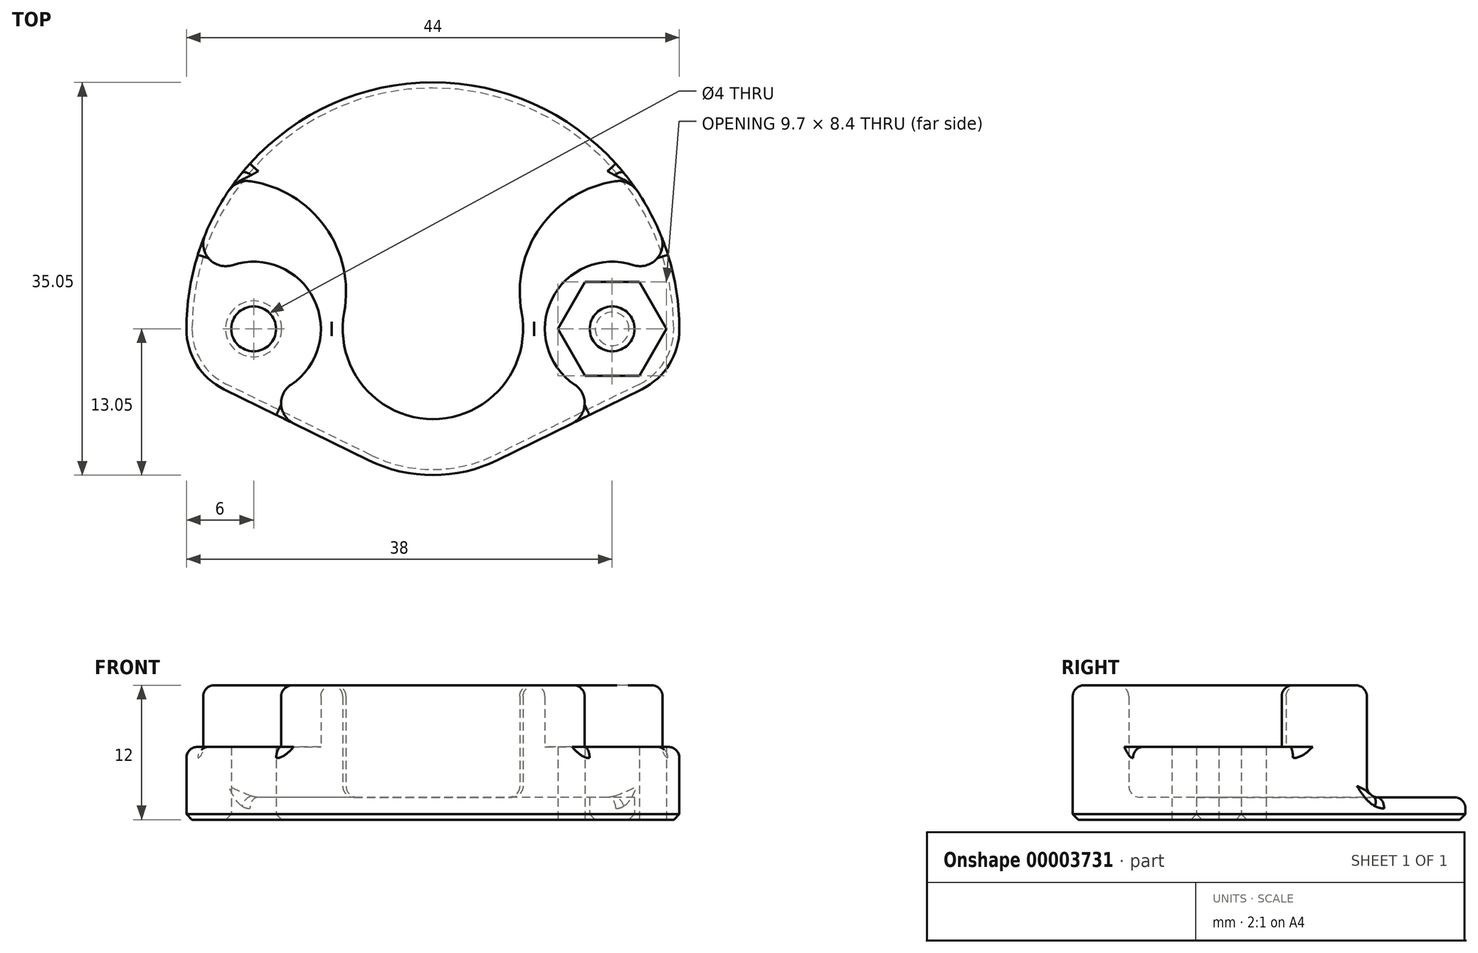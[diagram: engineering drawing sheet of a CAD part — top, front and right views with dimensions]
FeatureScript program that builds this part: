
annotation { "Feature Type Name" : "Feature", "Feature Type Description" : "" }
export const myFeature = defineFeature(function(context is Context, id is Id, definition is map)
    precondition{}
    {
        {
            var Q0;
            Q0=qCreatedBy(makeId("Top.planeOp"),FACE);
            var sketch = newSketch(context, id + "F0", { "sketchPlane" : qUnion([Q0])});
            skCircle(sketch, "E0", {"center": v(0, 0) * mm, "radius": 7.85 * mm, "construction": true});
            skCircle(sketch, "E1", {"center": v(-16, 0) * mm, "radius": 2 * mm});
            skLineSegment(sketch, "E2", {"start": v(0, 0) * mm, "end": v(0, -13.05) * mm, "construction": true});
            skCircle(sketch, "E3.MirrorC", {"center": v(16, 0) * mm, "radius": 2 * mm});
            skLineSegment(sketch, "E4", {"start": v(0, 0) * mm, "end": v(-11.3, 6.53) * mm, "construction": true});
            skLineSegment(sketch, "E5.MirrorCS", {"start": v(0, 0) * mm, "end": v(11.3, 6.53) * mm, "construction": true});
            skArc(sketch, "E6", {"start": v(-7.92, 1.47) * mm, "mid": v(0, -8.05) * mm, "end": v(7.92, 1.47) * mm});
            skArc(sketch, "E7.0", {"start": v(-9.43, 9.03) * mm, "mid": v(-12.85, -2.28) * mm, "end": v(-5.75, -11.71) * mm, "construction": true});
            skLineSegment(sketch, "E8", {"start": v(-18.64, -5.39) * mm, "end": v(-5.75, -11.71) * mm});
            skLineSegment(sketch, "E9", {"start": v(-8.77, 7.7) * mm, "end": v(-8.9, 7.94) * mm});
            skLineSegment(sketch, "E10", {"start": v(-16, 0) * mm, "end": v(0, 0) * mm, "construction": true});
            skLineSegment(sketch, "E11.MirrorCS", {"start": v(-18.64, 5.39) * mm, "end": v(-5.75, 11.71) * mm, "construction": true});
            skArc(sketch, "E12", {"start": v(-5.75, -11.71) * mm, "mid": v(0, -13.05) * mm, "end": v(5.75, -11.71) * mm});
            skLineSegment(sketch, "E13.MirrorCS", {"start": v(18.64, -5.39) * mm, "end": v(5.75, -11.71) * mm});
            skArc(sketch, "E14", {"start": v(5.75, -11.71) * mm, "mid": v(5.82, -11.68) * mm, "end": v(5.88, -11.65) * mm, "construction": true});
            skPoint(sketch, "E15.visualSharp", {"position": v(-6.97, 4.03) * mm});
            skArc(sketch, "E15.filletArc", {"start": v(-7.92, 1.47) * mm, "mid": v(-9.6, 9.1) * mm, "end": v(-16.28, 13.18) * mm});
            skPoint(sketch, "E16.visualSharp", {"position": v(6.97, 4.03) * mm});
            skArc(sketch, "E17.filletArc", {"start": v(-8.9, 7.94) * mm, "mid": v(-10.04, 8.95) * mm, "end": v(-11.57, 8.86) * mm, "construction": true});
            skArc(sketch, "E18.MirrorCS", {"start": v(-5.75, 11.71) * mm, "mid": v(0, 13.05) * mm, "end": v(5.75, 11.71) * mm, "construction": true});
            skLineSegment(sketch, "E19.MirrorCS", {"start": v(18.64, 5.39) * mm, "end": v(5.75, 11.71) * mm, "construction": true});
            skCircle(sketch, "E20.cCircle", {"center": v(-16, 0) * mm, "radius": 4.2 * mm, "construction": true});
            skLineSegment(sketch, "E20.0", {"start": v(-13.58, -4.2) * mm, "end": v(-18.42, -4.2) * mm});
            skLineSegment(sketch, "E20.1", {"start": v(-18.42, -4.2) * mm, "end": v(-20.85, 0) * mm});
            skLineSegment(sketch, "E20.2", {"start": v(-20.85, 0) * mm, "end": v(-18.42, 4.2) * mm});
            skLineSegment(sketch, "E20.3", {"start": v(-18.42, 4.2) * mm, "end": v(-13.58, 4.2) * mm});
            skLineSegment(sketch, "E20.4", {"start": v(-13.58, 4.2) * mm, "end": v(-11.15, 0) * mm});
            skLineSegment(sketch, "E20.5", {"start": v(-11.15, 0) * mm, "end": v(-13.58, -4.2) * mm});
            skPoint(sketch, "E20.0.midPoint", {"position": v(-16, -4.2) * mm});
            skLineSegment(sketch, "E21.MirrorCS", {"start": v(18.42, 4.2) * mm, "end": v(13.58, 4.2) * mm});
            skLineSegment(sketch, "E22.MirrorCS", {"start": v(13.58, 4.2) * mm, "end": v(11.15, 0) * mm});
            skLineSegment(sketch, "E23.MirrorCS", {"start": v(11.15, 0) * mm, "end": v(13.58, -4.2) * mm});
            skLineSegment(sketch, "E24.MirrorCS", {"start": v(13.58, -4.2) * mm, "end": v(18.42, -4.2) * mm});
            skLineSegment(sketch, "E25.MirrorCS", {"start": v(18.42, -4.2) * mm, "end": v(20.85, 0) * mm});
            skLineSegment(sketch, "E26.MirrorCS", {"start": v(20.85, 0) * mm, "end": v(18.42, 4.2) * mm});
            skCircle(sketch, "E27.converted", {"center": v(-16, 0) * mm, "radius": 6 * mm});
            skCircle(sketch, "E28.converted", {"center": v(16, 0) * mm, "radius": 6 * mm});
            skArc(sketch, "E29", {"start": v(-22, 0) * mm, "mid": v(0, 22) * mm, "end": v(22, 0) * mm});
            skPoint(sketch, "E30.newPointB", {"position": v(-22, 0) * mm});
            skArc(sketch, "E31", {"start": v(-16.28, 13.18) * mm, "mid": v(-17.38, 13.03) * mm, "end": v(-18.23, 12.32) * mm});
            skArc(sketch, "E32.MirrorCS", {"start": v(7.92, 1.47) * mm, "mid": v(9.6, 9.1) * mm, "end": v(16.28, 13.18) * mm});
            skArc(sketch, "E33.MirrorCS", {"start": v(16.28, 13.18) * mm, "mid": v(17.38, 13.03) * mm, "end": v(18.23, 12.32) * mm});
            skSolve(sketch);
        }
        {
            var Q0;
            Q0=makeQuery(id+"F0.imprint","IMPRINT",FACE,{"disambiguationData":[TD([[makeQuery(id+"F0.imprint","IMPRINT",EDGE,{"derivedFrom":sQuery(id+"F0.wireOp",EDGE,"E1")}),-1.0]])]});
            var Q1;
            Q1=makeQuery(id+"F0.imprint","IMPRINT",FACE,{"disambiguationData":[TD([[makeQuery(id+"F0.imprint","IMPRINT",EDGE,{"derivedFrom":sQuery(id+"F0.wireOp",EDGE,"E6")}),-1.0]])]});
            var Q2;
            Q2=makeQuery(id+"F0.imprint","IMPRINT",FACE,{"disambiguationData":[TD([[makeQuery(id+"F0.imprint","IMPRINT",EDGE,{"derivedFrom":sQuery(id+"F0.wireOp",EDGE,"E3.MirrorC")}),1.0]])]});
            var Q3;
            Q3=makeQuery(id+"F0.imprint","IMPRINT",FACE,{"disambiguationData":[TD([[makeQuery(id+"F0.imprint","IMPRINT",EDGE,{"derivedFrom":sQuery(id+"F0.wireOp",EDGE,"E6")}),1.0]])]});
            var Q4;
            Q4=makeQuery(id+"F0.imprint","IMPRINT",FACE,{"disambiguationData":[TD([[makeQuery(id+"F0.imprint","IMPRINT",EDGE,{"derivedFrom":sQuery(id+"F0.wireOp",EDGE,"E20.0")}),1.0]])]});
            var Q5;
            Q5=makeQuery(id+"F0.imprint","IMPRINT",FACE,{"disambiguationData":[TD([[makeQuery(id+"F0.imprint","IMPRINT",EDGE,{"derivedFrom":sQuery(id+"F0.wireOp",EDGE,"E21.MirrorCS")}),-1.0]])]});
            var Q6;
            {var subQ4=sQuery(id+"F0.wireOp",EDGE,"E18.MirrorCS");Q6=makeQuery(id+"F0.imprint","IMPRINT",FACE,{"disambiguationData":[TD([[makeQuery(id+"F0.imprint","IMPRINT",EDGE,{"derivedFrom":subQ4}),1.0]])]});}
            extrude(context, id + "F1", {"entities" : qUnion([Q0, Q1, Q2, Q3, Q4, Q5, Q6]), "depth" : 2 * mm});
        }
        {
            var Q0;
            Q0=makeQuery(id+"F0.imprint","IMPRINT",FACE,{"disambiguationData":[TD([[makeQuery(id+"F0.imprint","IMPRINT",EDGE,{"derivedFrom":sQuery(id+"F0.wireOp",EDGE,"E6")}),-1.0]])]});
            extrude(context, id + "F2", {"entities" : qUnion([Q0]), "operationType" : NewBodyOperationType.ADD, "depth" : 12 * mm});
        }
        {
            var Q0;
            Q0=makeQuery(id+"F0.imprint","IMPRINT",FACE,{"disambiguationData":[TD([[makeQuery(id+"F0.imprint","IMPRINT",EDGE,{"derivedFrom":sQuery(id+"F0.wireOp",EDGE,"E20.0")}),1.0]])]});
            var Q1;
            Q1=makeQuery(id+"F0.imprint","IMPRINT",FACE,{"disambiguationData":[TD([[makeQuery(id+"F0.imprint","IMPRINT",EDGE,{"derivedFrom":sQuery(id+"F0.wireOp",EDGE,"E21.MirrorCS")}),-1.0]])]});
            extrude(context, id + "F3", {"entities" : qUnion([Q0, Q1]), "operationType" : NewBodyOperationType.ADD, "depth" : (2 + 4.5) * mm});
        }
        {
            var Q0;
            Q0=makeQuery(id+"F3.boolean.opBoolean","SPLIT",EDGE,{"derivedFrom":makeQuery(id+"F2.opExtrude","SWEPT_EDGE",EDGE,{"disambiguationData":[OSD([sQuery(id+"F0.wireOp",EDGE,"E11.MirrorCS"),sQuery(id+"F0.wireOp",EDGE,"E27.converted")])]})});
            var Q1;
            Q1=makeQuery(id+"F3.boolean.opBoolean","SPLIT",EDGE,{"derivedFrom":makeQuery(id+"F2.opExtrude","SWEPT_EDGE",EDGE,{"disambiguationData":[OSD([sQuery(id+"F0.wireOp",EDGE,"E8"),sQuery(id+"F0.wireOp",EDGE,"E27.converted")])]})});
            var Q2;
            Q2=makeQuery(id+"F3.boolean.opBoolean","SPLIT",EDGE,{"derivedFrom":makeQuery(id+"F2.opExtrude","SWEPT_EDGE",EDGE,{"disambiguationData":[OSD([sQuery(id+"F0.wireOp",EDGE,"E19.MirrorCS"),sQuery(id+"F0.wireOp",EDGE,"E28.converted")])]})});
            var Q3;
            Q3=makeQuery(id+"F3.boolean.opBoolean","SPLIT",EDGE,{"derivedFrom":makeQuery(id+"F2.opExtrude","SWEPT_EDGE",EDGE,{"disambiguationData":[OSD([sQuery(id+"F0.wireOp",EDGE,"E13.MirrorCS"),sQuery(id+"F0.wireOp",EDGE,"E28.converted")])]})});
            fillet(context, id + "F4", {"entities" : qUnion([Q0, Q1, Q2, Q3]), "radius" : 2 * mm, "tangentPropagation" : true, "allowEdgeOverflow" : false});
        }
        {
            var Q0;
            {var subQ0=sQuery(id+"F0.wireOp",EDGE,"E11.MirrorCS");var subQ1=sQuery(id+"F0.wireOp",EDGE,"wUdlfTOz-FRgl-y8Ec-oWtE-mNZlK31t2N4R");Q0=makeQuery(id+"F4.opFillet","BLEND_EDGE",EDGE,{"blendedFrom":[makeQuery(id+"F2.opExtrude","SWEPT_EDGE",EDGE,{"disambiguationData":[OSD([subQ1,subQ0])]}),makeQuery(id+"F2.opExtrude","CAP_FACE",FACE,{"disambiguationData":[OSD([sQuery(id+"F0.wireOp",EDGE,"E6"),subQ1,sQuery(id+"F0.wireOp",EDGE,"E8"),sQuery(id+"F0.wireOp",EDGE,"E9"),sQuery(id+"F0.wireOp",EDGE,"ff612a64-ed8f-42e0-9850-7b6d3d933fa10.MirrorCS"),subQ0,sQuery(id+"F0.wireOp",EDGE,"E12"),sQuery(id+"F0.wireOp",EDGE,"362a2e85-9377-49f7-9ba6-55e35935365c0.MirrorC"),sQuery(id+"F0.wireOp",EDGE,"c10635a2-e605-4d98-a689-4e845083322d0.MirrorCS"),sQuery(id+"F0.wireOp",EDGE,"E13.MirrorCS"),sQuery(id+"F0.wireOp",EDGE,"E15.filletArc"),sQuery(id+"F0.wireOp",EDGE,"E16.filletArc"),sQuery(id+"F0.wireOp",EDGE,"E17.filletArc"),sQuery(id+"F0.wireOp",EDGE,"e15231d0-0402-4fd1-8143-67f33edc8a02.filletArc")])],"isStart":false})],"blendedInto":[makeQuery(id+"F2.opExtrude","CAP_FACE",FACE,{"disambiguationData":[OSD([sQuery(id+"F0.wireOp",EDGE,"E6"),subQ1,sQuery(id+"F0.wireOp",EDGE,"E8"),sQuery(id+"F0.wireOp",EDGE,"E9"),sQuery(id+"F0.wireOp",EDGE,"ff612a64-ed8f-42e0-9850-7b6d3d933fa10.MirrorCS"),subQ0,sQuery(id+"F0.wireOp",EDGE,"E12"),sQuery(id+"F0.wireOp",EDGE,"362a2e85-9377-49f7-9ba6-55e35935365c0.MirrorC"),sQuery(id+"F0.wireOp",EDGE,"c10635a2-e605-4d98-a689-4e845083322d0.MirrorCS"),sQuery(id+"F0.wireOp",EDGE,"E13.MirrorCS"),sQuery(id+"F0.wireOp",EDGE,"E15.filletArc"),sQuery(id+"F0.wireOp",EDGE,"E16.filletArc"),sQuery(id+"F0.wireOp",EDGE,"E17.filletArc"),sQuery(id+"F0.wireOp",EDGE,"e15231d0-0402-4fd1-8143-67f33edc8a02.filletArc")])],"isStart":false})]});}
            var Q1;
            Q1=makeQuery(id+"F1.opExtrude","CAP_EDGE",EDGE,{"disambiguationData":[OSD([sQuery(id+"F0.wireOp",EDGE,"wUdlfTOz-FRgl-y8Ec-oWtE-mNZlK31t2N4R")])],"isStart":false});
            var Q2;
            Q2=makeQuery(id+"F1.opExtrude","CAP_EDGE",EDGE,{"disambiguationData":[OSD([sQuery(id+"F0.wireOp",EDGE,"362a2e85-9377-49f7-9ba6-55e35935365c0.MirrorC")])],"isStart":false});
            var Q3;
            {var subQ0=sQuery(id+"F0.wireOp",EDGE,"E11.MirrorCS");var subQ1=sQuery(id+"F0.wireOp",EDGE,"E8");var subQ2=sQuery(id+"F0.wireOp",EDGE,"wUdlfTOz-FRgl-y8Ec-oWtE-mNZlK31t2N4R");var subQ3=sQuery(id+"F0.wireOp",EDGE,"E1");Q3=makeQuery(id+"F4.opFillet","BLEND_EDGE",EDGE,{"blendedFrom":[makeQuery(id+"F2.opExtrude","SWEPT_EDGE",EDGE,{"disambiguationData":[OSD([subQ2,subQ1])]}),makeQuery(id+"F2.boolean.opBoolean","SPLIT",FACE,{"disambiguationData":[TD([makeQuery(id+"F1.opExtrude","SWEPT_FACE",FACE,{"disambiguationData":[OSD([subQ3])]})])],"derivedFrom":makeQuery(id+"F1.opExtrude","CAP_FACE",FACE,{"disambiguationData":[OSD([subQ3,sQuery(id+"F0.wireOp",EDGE,"E3.MirrorC"),sQuery(id+"F0.wireOp",EDGE,"E6"),subQ2,subQ1,sQuery(id+"F0.wireOp",EDGE,"E9"),sQuery(id+"F0.wireOp",EDGE,"ff612a64-ed8f-42e0-9850-7b6d3d933fa10.MirrorCS"),subQ0,sQuery(id+"F0.wireOp",EDGE,"E12"),sQuery(id+"F0.wireOp",EDGE,"362a2e85-9377-49f7-9ba6-55e35935365c0.MirrorC"),sQuery(id+"F0.wireOp",EDGE,"c10635a2-e605-4d98-a689-4e845083322d0.MirrorCS"),sQuery(id+"F0.wireOp",EDGE,"E13.MirrorCS"),sQuery(id+"F0.wireOp",EDGE,"E15.filletArc"),sQuery(id+"F0.wireOp",EDGE,"E16.filletArc"),sQuery(id+"F0.wireOp",EDGE,"E17.filletArc"),sQuery(id+"F0.wireOp",EDGE,"e15231d0-0402-4fd1-8143-67f33edc8a02.filletArc")])],"isStart":false})})],"blendedInto":[makeQuery(id+"F2.boolean.opBoolean","SPLIT",FACE,{"disambiguationData":[TD([makeQuery(id+"F1.opExtrude","SWEPT_FACE",FACE,{"disambiguationData":[OSD([subQ3])]})])],"derivedFrom":makeQuery(id+"F1.opExtrude","CAP_FACE",FACE,{"disambiguationData":[OSD([subQ3,sQuery(id+"F0.wireOp",EDGE,"E3.MirrorC"),sQuery(id+"F0.wireOp",EDGE,"E6"),subQ2,subQ1,sQuery(id+"F0.wireOp",EDGE,"E9"),sQuery(id+"F0.wireOp",EDGE,"ff612a64-ed8f-42e0-9850-7b6d3d933fa10.MirrorCS"),subQ0,sQuery(id+"F0.wireOp",EDGE,"E12"),sQuery(id+"F0.wireOp",EDGE,"362a2e85-9377-49f7-9ba6-55e35935365c0.MirrorC"),sQuery(id+"F0.wireOp",EDGE,"c10635a2-e605-4d98-a689-4e845083322d0.MirrorCS"),sQuery(id+"F0.wireOp",EDGE,"E13.MirrorCS"),sQuery(id+"F0.wireOp",EDGE,"E15.filletArc"),sQuery(id+"F0.wireOp",EDGE,"E16.filletArc"),sQuery(id+"F0.wireOp",EDGE,"E17.filletArc"),sQuery(id+"F0.wireOp",EDGE,"e15231d0-0402-4fd1-8143-67f33edc8a02.filletArc")])],"isStart":false})})]});}
            var Q4;
            {var subQ0=sQuery(id+"F0.wireOp",EDGE,"E13.MirrorCS");var subQ1=sQuery(id+"F0.wireOp",EDGE,"362a2e85-9377-49f7-9ba6-55e35935365c0.MirrorC");var subQ2=sQuery(id+"F0.wireOp",EDGE,"c10635a2-e605-4d98-a689-4e845083322d0.MirrorCS");var subQ3=sQuery(id+"F0.wireOp",EDGE,"E3.MirrorC");Q4=makeQuery(id+"F4.opFillet","BLEND_EDGE",EDGE,{"blendedFrom":[makeQuery(id+"F2.opExtrude","SWEPT_EDGE",EDGE,{"disambiguationData":[OSD([subQ1,subQ0])]}),makeQuery(id+"F2.boolean.opBoolean","SPLIT",FACE,{"disambiguationData":[TD([makeQuery(id+"F1.opExtrude","SWEPT_FACE",FACE,{"disambiguationData":[OSD([subQ3])]})])],"derivedFrom":makeQuery(id+"F1.opExtrude","CAP_FACE",FACE,{"disambiguationData":[OSD([sQuery(id+"F0.wireOp",EDGE,"E1"),subQ3,sQuery(id+"F0.wireOp",EDGE,"E6"),sQuery(id+"F0.wireOp",EDGE,"wUdlfTOz-FRgl-y8Ec-oWtE-mNZlK31t2N4R"),sQuery(id+"F0.wireOp",EDGE,"E8"),sQuery(id+"F0.wireOp",EDGE,"E9"),sQuery(id+"F0.wireOp",EDGE,"ff612a64-ed8f-42e0-9850-7b6d3d933fa10.MirrorCS"),sQuery(id+"F0.wireOp",EDGE,"E11.MirrorCS"),sQuery(id+"F0.wireOp",EDGE,"E12"),subQ1,subQ2,subQ0,sQuery(id+"F0.wireOp",EDGE,"E15.filletArc"),sQuery(id+"F0.wireOp",EDGE,"E16.filletArc"),sQuery(id+"F0.wireOp",EDGE,"E17.filletArc"),sQuery(id+"F0.wireOp",EDGE,"e15231d0-0402-4fd1-8143-67f33edc8a02.filletArc")])],"isStart":false})})],"blendedInto":[makeQuery(id+"F2.boolean.opBoolean","SPLIT",FACE,{"disambiguationData":[TD([makeQuery(id+"F1.opExtrude","SWEPT_FACE",FACE,{"disambiguationData":[OSD([subQ3])]})])],"derivedFrom":makeQuery(id+"F1.opExtrude","CAP_FACE",FACE,{"disambiguationData":[OSD([sQuery(id+"F0.wireOp",EDGE,"E1"),subQ3,sQuery(id+"F0.wireOp",EDGE,"E6"),sQuery(id+"F0.wireOp",EDGE,"wUdlfTOz-FRgl-y8Ec-oWtE-mNZlK31t2N4R"),sQuery(id+"F0.wireOp",EDGE,"E8"),sQuery(id+"F0.wireOp",EDGE,"E9"),sQuery(id+"F0.wireOp",EDGE,"ff612a64-ed8f-42e0-9850-7b6d3d933fa10.MirrorCS"),sQuery(id+"F0.wireOp",EDGE,"E11.MirrorCS"),sQuery(id+"F0.wireOp",EDGE,"E12"),subQ1,subQ2,subQ0,sQuery(id+"F0.wireOp",EDGE,"E15.filletArc"),sQuery(id+"F0.wireOp",EDGE,"E16.filletArc"),sQuery(id+"F0.wireOp",EDGE,"E17.filletArc"),sQuery(id+"F0.wireOp",EDGE,"e15231d0-0402-4fd1-8143-67f33edc8a02.filletArc")])],"isStart":false})})]});}
            var Q5;
            Q5=makeQuery(id+"F1.opExtrude","CAP_EDGE",EDGE,{"disambiguationData":[OSD([sQuery(id+"F0.wireOp",EDGE,"E18.MirrorCS")])],"isStart":false});
            var Q6;
            Q6=makeQuery(id+"F3.boolean.opBoolean","SPLIT",EDGE,{"disambiguationData":[OD(0.0)],"derivedFrom":makeQuery(id+"F3.opExtrude","CAP_EDGE",EDGE,{"disambiguationData":[OSD([sQuery(id+"F0.wireOp",EDGE,"E27.converted")])],"isStart":false})});
            var Q7;
            Q7=makeQuery(id+"F3.boolean.opBoolean","SPLIT",EDGE,{"disambiguationData":[OD(0.0)],"derivedFrom":makeQuery(id+"F3.opExtrude","CAP_EDGE",EDGE,{"disambiguationData":[OSD([sQuery(id+"F0.wireOp",EDGE,"E28.converted")])],"isStart":false})});
            var Q8;
            Q8=makeQuery(id+"F3.boolean.opBoolean","SPLIT",EDGE,{"disambiguationData":[OD(1.0)],"derivedFrom":makeQuery(id+"F3.opExtrude","CAP_EDGE",EDGE,{"disambiguationData":[OSD([sQuery(id+"F0.wireOp",EDGE,"E27.converted")])],"isStart":false})});
            var Q9;
            Q9=makeQuery(id+"F3.boolean.opBoolean","SPLIT",EDGE,{"disambiguationData":[OD(1.0)],"derivedFrom":makeQuery(id+"F3.opExtrude","CAP_EDGE",EDGE,{"disambiguationData":[OSD([sQuery(id+"F0.wireOp",EDGE,"E28.converted")])],"isStart":false})});
            var Q10;
            Q10=makeQuery(id+"F1.opExtrude","CAP_EDGE",EDGE,{"disambiguationData":[OSD([sQuery(id+"F0.wireOp",EDGE,"E29")])],"isStart":false});
            var Q11;
            Q11=makeQuery(id+"F2.boolean.opBoolean","INTERSECT",EDGE,{"derivedFrom":[makeQuery(id+"F1.opExtrude","CAP_FACE",FACE,{"disambiguationData":[OSD([sQuery(id+"F0.wireOp",EDGE,"E1"),sQuery(id+"F0.wireOp",EDGE,"E3.MirrorC"),sQuery(id+"F0.wireOp",EDGE,"E8"),sQuery(id+"F0.wireOp",EDGE,"E12"),sQuery(id+"F0.wireOp",EDGE,"E13.MirrorCS"),sQuery(id+"F0.wireOp",EDGE,"E27.converted"),sQuery(id+"F0.wireOp",EDGE,"E28.converted"),sQuery(id+"F0.wireOp",EDGE,"E29")])],"isStart":false}),makeQuery(id+"F2.opExtrude","SWEPT_FACE",FACE,{"disambiguationData":[OSD([sQuery(id+"F0.wireOp",EDGE,"E6")])]})]});
            var Q12;
            {var subQ0=sQuery(id+"F0.wireOp",EDGE,"E29");var subQ1=sQuery(id+"F0.wireOp",EDGE,"E27.converted");Q12=makeQuery(id+"F4.opFillet","BLEND_EDGE",EDGE,{"blendedFrom":[makeQuery(id+"F3.boolean.opBoolean","SPLIT",EDGE,{"derivedFrom":makeQuery(id+"F2.opExtrude","SWEPT_EDGE",EDGE,{"disambiguationData":[OSD([subQ1,subQ0])]})}),makeQuery(id+"F2.opExtrude","CAP_FACE",FACE,{"disambiguationData":[OSD([sQuery(id+"F0.wireOp",EDGE,"E6"),sQuery(id+"F0.wireOp",EDGE,"E8"),sQuery(id+"F0.wireOp",EDGE,"E12"),sQuery(id+"F0.wireOp",EDGE,"E13.MirrorCS"),sQuery(id+"F0.wireOp",EDGE,"E15.filletArc"),subQ1,sQuery(id+"F0.wireOp",EDGE,"E28.converted"),subQ0,sQuery(id+"F0.wireOp",EDGE,"E31"),sQuery(id+"F0.wireOp",EDGE,"E32.MirrorCS"),sQuery(id+"F0.wireOp",EDGE,"E33.MirrorCS")])],"isStart":false})],"blendedInto":[makeQuery(id+"F2.opExtrude","CAP_FACE",FACE,{"disambiguationData":[OSD([sQuery(id+"F0.wireOp",EDGE,"E6"),sQuery(id+"F0.wireOp",EDGE,"E8"),sQuery(id+"F0.wireOp",EDGE,"E12"),sQuery(id+"F0.wireOp",EDGE,"E13.MirrorCS"),sQuery(id+"F0.wireOp",EDGE,"E15.filletArc"),subQ1,sQuery(id+"F0.wireOp",EDGE,"E28.converted"),subQ0,sQuery(id+"F0.wireOp",EDGE,"E31"),sQuery(id+"F0.wireOp",EDGE,"E32.MirrorCS"),sQuery(id+"F0.wireOp",EDGE,"E33.MirrorCS")])],"isStart":false})]});}
            fillet(context, id + "F5", {"entities" : qUnion([Q0, Q1, Q2, Q3, Q4, Q5, Q6, Q7, Q8, Q9, Q10, Q11, Q12]), "radius" : 1 * mm, "tangentPropagation" : true, "allowEdgeOverflow" : false});
        }
        {
            var Q0;
            Q0=makeQuery(id+"F1.opExtrude","CAP_EDGE",EDGE,{"disambiguationData":[OSD([sQuery(id+"F0.wireOp",EDGE,"E12")])],"isStart":true});
            var Q1;
            Q1=makeQuery(id+"F1.opExtrude","CAP_EDGE",EDGE,{"disambiguationData":[OSD([sQuery(id+"F0.wireOp",EDGE,"E1")])],"isStart":true});
            var Q2;
            Q2=makeQuery(id+"F1.opExtrude","CAP_EDGE",EDGE,{"disambiguationData":[OSD([sQuery(id+"F0.wireOp",EDGE,"E3.MirrorC")])],"isStart":true});
            chamfer(context, id + "F6", {"entities" : qUnion([Q0, Q1, Q2]), "width" : 0.5 * mm, "tangentPropagation" : true});
        }
        {
            var Q0;
            {var subQ0=sQuery(id+"F0.wireOp",EDGE,"E29");var subQ1=sQuery(id+"F0.wireOp",EDGE,"E27.converted");var subQ2=sQuery(id+"F0.wireOp",EDGE,"E8");var subQ3=sQuery(id+"F0.wireOp",EDGE,"E28.converted");var subQ4=sQuery(id+"F0.wireOp",EDGE,"E1");Q0=makeQuery(id+"F2.boolean.opBoolean","SPLIT",FACE,{"disambiguationData":[TD([makeQuery(id+"F1.opExtrude","SWEPT_FACE",FACE,{"disambiguationData":[OSD([subQ4])]})])],"derivedFrom":makeQuery(id+"F1.opExtrude","CAP_FACE",FACE,{"disambiguationData":[OSD([subQ4,sQuery(id+"F0.wireOp",EDGE,"E3.MirrorC"),subQ2,sQuery(id+"F0.wireOp",EDGE,"E12"),sQuery(id+"F0.wireOp",EDGE,"E13.MirrorCS"),subQ1,subQ3,subQ0])],"isStart":false})});}
            var Q1;
            {var subQ0=sQuery(id+"F0.wireOp",EDGE,"E13.MirrorCS");var subQ1=sQuery(id+"F0.wireOp",EDGE,"E29");var subQ2=sQuery(id+"F0.wireOp",EDGE,"E28.converted");var subQ3=sQuery(id+"F0.wireOp",EDGE,"E3.MirrorC");var subQ4=sQuery(id+"F0.wireOp",EDGE,"E27.converted");Q1=makeQuery(id+"F2.boolean.opBoolean","SPLIT",FACE,{"disambiguationData":[TD([makeQuery(id+"F1.opExtrude","SWEPT_FACE",FACE,{"disambiguationData":[OSD([subQ3])]})])],"derivedFrom":makeQuery(id+"F1.opExtrude","CAP_FACE",FACE,{"disambiguationData":[OSD([sQuery(id+"F0.wireOp",EDGE,"E1"),subQ3,sQuery(id+"F0.wireOp",EDGE,"E8"),sQuery(id+"F0.wireOp",EDGE,"E12"),subQ0,subQ4,subQ2,subQ1])],"isStart":false})});}
            var Q2;
            Q2=makeQuery(id+"F3.opExtrude","CAP_FACE",FACE,{"disambiguationData":[OSD([sQuery(id+"F0.wireOp",EDGE,"E20.0"),sQuery(id+"F0.wireOp",EDGE,"E20.1"),sQuery(id+"F0.wireOp",EDGE,"E20.2"),sQuery(id+"F0.wireOp",EDGE,"E20.3"),sQuery(id+"F0.wireOp",EDGE,"E20.4"),sQuery(id+"F0.wireOp",EDGE,"E20.5"),sQuery(id+"F0.wireOp",EDGE,"E27.converted")])],"isStart":false});
            extrude(context, id + "F7", {"entities" : qUnion([Q0, Q1]), "operationType" : NewBodyOperationType.ADD, "endBound" : BoundingType.UP_TO_SURFACE, "endBoundEntityFace" : qUnion([Q2]), "depth" : 25 * mm});
        }
    });
